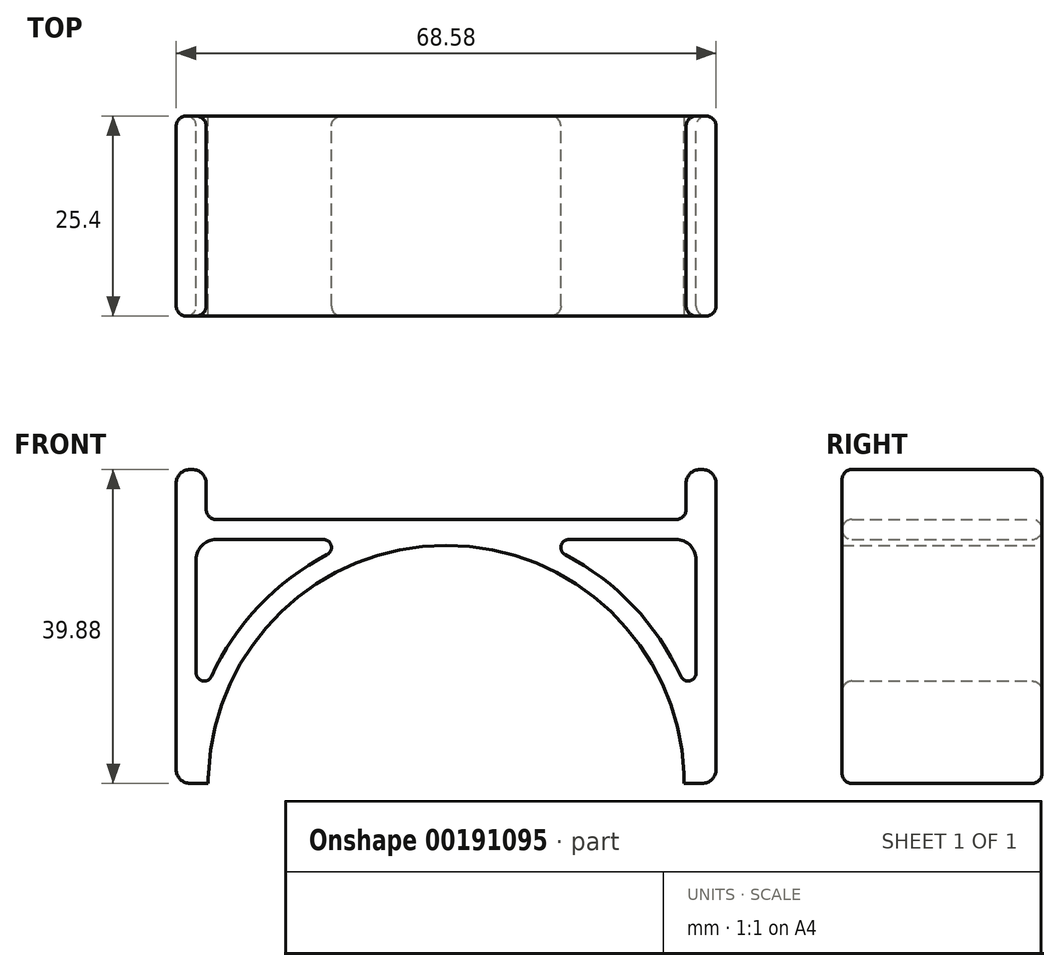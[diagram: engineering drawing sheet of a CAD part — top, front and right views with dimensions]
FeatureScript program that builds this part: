
annotation { "Feature Type Name" : "Feature", "Feature Type Description" : "" }
export const myFeature = defineFeature(function(context is Context, id is Id, definition is map)
    precondition{}
    {
        {
            var Q0;
            Q0=qCreatedBy(makeId("Front.planeOp"),FACE);
            var sketch = newSketch(context, id + "F0", { "sketchPlane" : qUnion([Q0])});
            skArc(sketch, "E0", {"start": v(30.23, 0) * mm, "mid": v(21.37, 21.37) * mm, "end": v(0, 30.23) * mm});
            skLineSegment(sketch, "E1", {"start": v(0, 33.53) * mm, "end": v(30.48, 33.53) * mm});
            skLineSegment(sketch, "E2", {"start": v(30.48, 33.53) * mm, "end": v(30.48, 39.88) * mm});
            skLineSegment(sketch, "E3", {"start": v(30.48, 39.88) * mm, "end": v(34.3, 39.88) * mm});
            skLineSegment(sketch, "E4", {"start": v(34.3, 39.88) * mm, "end": v(34.3, 0) * mm});
            skLineSegment(sketch, "E5", {"start": v(0, 0) * mm, "end": v(0, 49.35) * mm, "construction": true});
            skPoint(sketch, "E6.orphan", {"position": v(-30.48, 33.53) * mm});
            skLineSegment(sketch, "E7", {"start": v(34.3, 0) * mm, "end": v(30.23, 0) * mm});
            skArc(sketch, "E8", {"start": v(31.75, 8.1) * mm, "mid": v(24.1, 22.2) * mm, "end": v(10.65, 30.99) * mm});
            skLineSegment(sketch, "E9", {"start": v(31.75, 30.99) * mm, "end": v(10.65, 30.99) * mm});
            skLineSegment(sketch, "E10", {"start": v(31.75, 30.99) * mm, "end": v(31.75, 8.1) * mm});
            skLineSegment(sketch, "E11.MirrorCS", {"start": v(0, 33.53) * mm, "end": v(-30.48, 33.53) * mm});
            skLineSegment(sketch, "E12.MirrorCS", {"start": v(-30.48, 33.53) * mm, "end": v(-30.48, 39.88) * mm});
            skLineSegment(sketch, "E13.MirrorCS", {"start": v(-30.48, 39.88) * mm, "end": v(-34.3, 39.88) * mm});
            skLineSegment(sketch, "E14.MirrorCS", {"start": v(-34.3, 39.88) * mm, "end": v(-34.3, 0) * mm});
            skLineSegment(sketch, "E15.MirrorCS", {"start": v(-34.3, 0) * mm, "end": v(-30.23, 0) * mm});
            skArc(sketch, "E16.MirrorCS", {"start": v(-30.23, 0) * mm, "mid": v(-21.37, 21.37) * mm, "end": v(0, 30.23) * mm});
            skArc(sketch, "E17.MirrorCS", {"start": v(-31.75, 8.1) * mm, "mid": v(-24.1, 22.2) * mm, "end": v(-10.65, 30.99) * mm});
            skLineSegment(sketch, "E18.MirrorCS", {"start": v(-31.75, 30.99) * mm, "end": v(-10.65, 30.99) * mm});
            skLineSegment(sketch, "E19.MirrorCS", {"start": v(-31.75, 30.99) * mm, "end": v(-31.75, 8.1) * mm});
            skSolve(sketch);
        }
        {
            var Q0;
            Q0 = qSketchRegion(id + "F0", true);
            extrude(context, id + "F1", {"entities" : qUnion([Q0]), "depth" : 25.4 * mm});
        }
        {
            var Q0;
            Q0=makeQuery(id+"F1.opExtrude","SWEPT_EDGE",EDGE,{"disambiguationData":[OSD([sQuery(id+"F0.wireOp",EDGE,"E12.MirrorCS"),sQuery(id+"F0.wireOp",EDGE,"E13.MirrorCS")])]});
            var Q1;
            Q1=makeQuery(id+"F1.opExtrude","SWEPT_EDGE",EDGE,{"disambiguationData":[OSD([sQuery(id+"F0.wireOp",EDGE,"E13.MirrorCS"),sQuery(id+"F0.wireOp",EDGE,"E14.MirrorCS")])]});
            var Q2;
            Q2=makeQuery(id+"F1.opExtrude","SWEPT_EDGE",EDGE,{"disambiguationData":[OSD([sQuery(id+"F0.wireOp",EDGE,"E3"),sQuery(id+"F0.wireOp",EDGE,"E4")])]});
            var Q3;
            Q3=makeQuery(id+"F1.opExtrude","SWEPT_EDGE",EDGE,{"disambiguationData":[OSD([sQuery(id+"F0.wireOp",EDGE,"E2"),sQuery(id+"F0.wireOp",EDGE,"E3")])]});
            var Q4;
            Q4=makeQuery(id+"F1.opExtrude","SWEPT_EDGE",EDGE,{"disambiguationData":[OSD([sQuery(id+"F0.wireOp",EDGE,"E4"),sQuery(id+"F0.wireOp",EDGE,"E7")])]});
            var Q5;
            Q5=makeQuery(id+"F1.opExtrude","SWEPT_EDGE",EDGE,{"disambiguationData":[OSD([sQuery(id+"F0.wireOp",EDGE,"E14.MirrorCS"),sQuery(id+"F0.wireOp",EDGE,"E15.MirrorCS")])]});
            fillet(context, id + "F2", {"entities" : qUnion([Q0, Q1, Q2, Q3, Q4, Q5]), "radius" : 1.78 * mm, "tangentPropagation" : true, "allowEdgeOverflow" : false});
        }
        {
            var Q0;
            Q0=makeQuery(id+"F1.opExtrude","SWEPT_EDGE",EDGE,{"disambiguationData":[OSD([sQuery(id+"F0.wireOp",EDGE,"E18.MirrorCS"),sQuery(id+"F0.wireOp",EDGE,"E19.MirrorCS")])]});
            var Q1;
            Q1=makeQuery(id+"F1.opExtrude","SWEPT_EDGE",EDGE,{"disambiguationData":[OSD([sQuery(id+"F0.wireOp",EDGE,"E9"),sQuery(id+"F0.wireOp",EDGE,"E10")])]});
            fillet(context, id + "F3", {"entities" : qUnion([Q0, Q1]), "radius" : 2.54 * mm, "tangentPropagation" : true, "allowEdgeOverflow" : false});
        }
        {
            var Q0;
            Q0=makeQuery(id+"F1.opExtrude","SWEPT_EDGE",EDGE,{"disambiguationData":[OSD([sQuery(id+"F0.wireOp",EDGE,"E17.MirrorCS"),sQuery(id+"F0.wireOp",EDGE,"E18.MirrorCS")])]});
            var Q1;
            Q1=makeQuery(id+"F1.opExtrude","SWEPT_EDGE",EDGE,{"disambiguationData":[OSD([sQuery(id+"F0.wireOp",EDGE,"E17.MirrorCS"),sQuery(id+"F0.wireOp",EDGE,"E19.MirrorCS")])]});
            var Q2;
            Q2=makeQuery(id+"F1.opExtrude","SWEPT_EDGE",EDGE,{"disambiguationData":[OSD([sQuery(id+"F0.wireOp",EDGE,"E8"),sQuery(id+"F0.wireOp",EDGE,"E10")])]});
            var Q3;
            Q3=makeQuery(id+"F1.opExtrude","SWEPT_EDGE",EDGE,{"disambiguationData":[OSD([sQuery(id+"F0.wireOp",EDGE,"E8"),sQuery(id+"F0.wireOp",EDGE,"E9")])]});
            fillet(context, id + "F4", {"entities" : qUnion([Q0, Q1, Q2, Q3]), "radius" : 1.02 * mm, "tangentPropagation" : true, "allowEdgeOverflow" : false});
        }
        {
            var Q0;
            Q0=makeQuery(id+"F1.opExtrude","SWEPT_EDGE",EDGE,{"disambiguationData":[OSD([sQuery(id+"F0.wireOp",EDGE,"E11.MirrorCS"),sQuery(id+"F0.wireOp",EDGE,"E12.MirrorCS")])]});
            var Q1;
            Q1=makeQuery(id+"F1.opExtrude","SWEPT_EDGE",EDGE,{"disambiguationData":[OSD([sQuery(id+"F0.wireOp",EDGE,"E1"),sQuery(id+"F0.wireOp",EDGE,"E2")])]});
            fillet(context, id + "F5", {"entities" : qUnion([Q0, Q1]), "radius" : 1.27 * mm, "tangentPropagation" : true, "allowEdgeOverflow" : false});
        }
        {
            var Q0;
            Q0=makeQuery(id+"F1.opExtrude","CAP_EDGE",EDGE,{"disambiguationData":[OSD([sQuery(id+"F0.wireOp",EDGE,"E14.MirrorCS")])],"isStart":false});
            var Q1;
            Q1=makeQuery(id+"F1.opExtrude","CAP_EDGE",EDGE,{"disambiguationData":[OSD([sQuery(id+"F0.wireOp",EDGE,"E17.MirrorCS")])],"isStart":false});
            var Q2;
            Q2=makeQuery(id+"F1.opExtrude","CAP_EDGE",EDGE,{"disambiguationData":[OSD([sQuery(id+"F0.wireOp",EDGE,"E8")])],"isStart":false});
            var Q3;
            Q3=makeQuery(id+"F1.opExtrude","CAP_EDGE",EDGE,{"disambiguationData":[OSD([sQuery(id+"F0.wireOp",EDGE,"E1"),sQuery(id+"F0.wireOp",EDGE,"E11.MirrorCS")])],"isStart":true});
            var Q4;
            Q4=makeQuery(id+"F1.opExtrude","CAP_EDGE",EDGE,{"disambiguationData":[OSD([sQuery(id+"F0.wireOp",EDGE,"E10")])],"isStart":true});
            var Q5;
            Q5=makeQuery(id+"F1.opExtrude","CAP_EDGE",EDGE,{"disambiguationData":[OSD([sQuery(id+"F0.wireOp",EDGE,"E17.MirrorCS")])],"isStart":true});
            fillet(context, id + "F6", {"entities" : qUnion([Q0, Q1, Q2, Q3, Q4, Q5]), "radius" : 1.27 * mm, "tangentPropagation" : true, "allowEdgeOverflow" : false});
        }
    });
